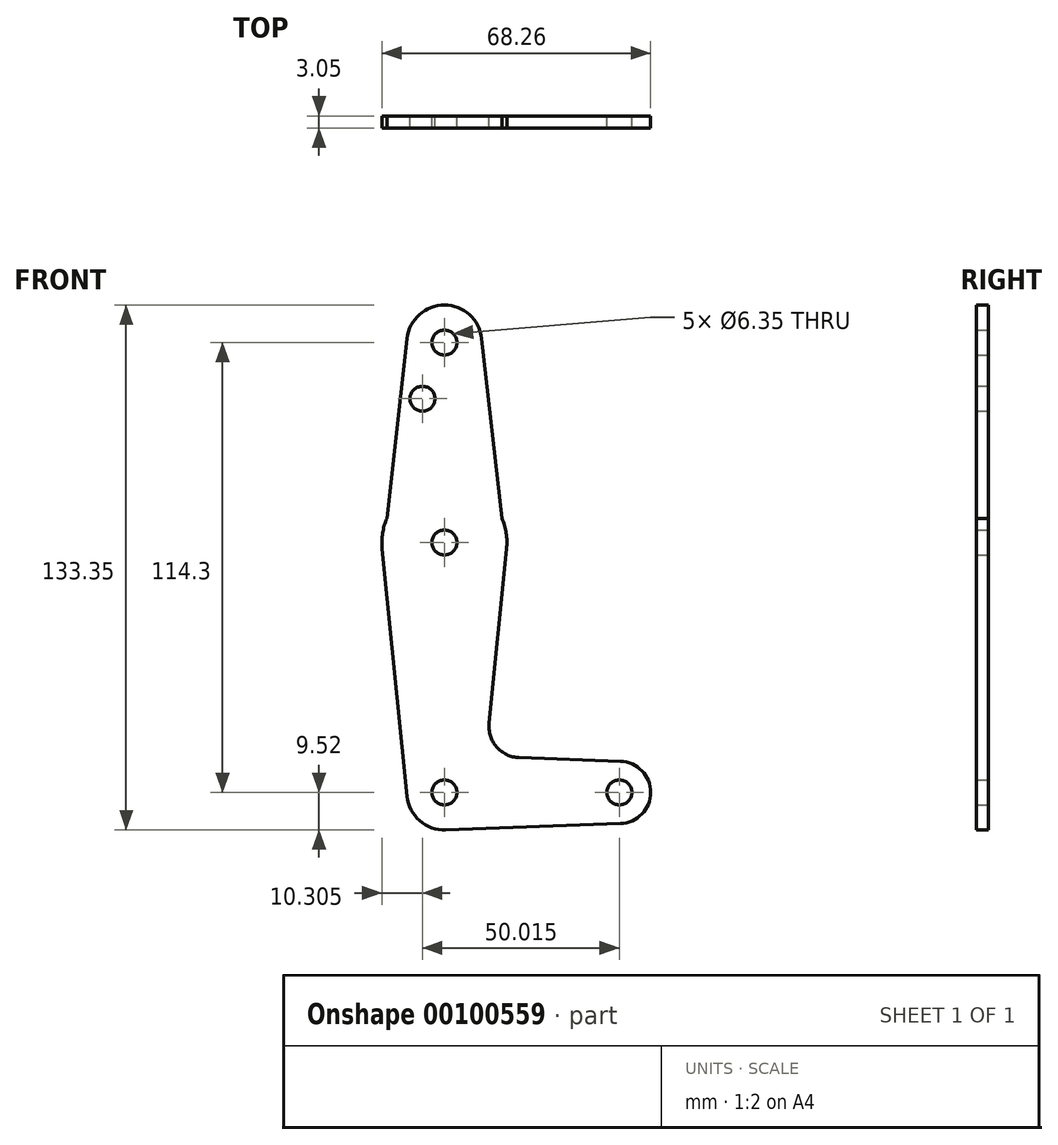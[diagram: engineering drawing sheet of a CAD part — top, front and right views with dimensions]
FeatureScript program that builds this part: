
annotation { "Feature Type Name" : "Feature", "Feature Type Description" : "" }
export const myFeature = defineFeature(function(context is Context, id is Id, definition is map)
    precondition{}
    {
        {
            var Q0;
            Q0=qCreatedBy(makeId("Front.planeOp"),FACE);
            var sketch = newSketch(context, id + "F0", { "sketchPlane" : qUnion([Q0])});
            skLineSegment(sketch, "E0", {"start": v(0, 0) * mm, "end": v(0, 114.3) * mm, "construction": true});
            skLineSegment(sketch, "E1", {"start": v(0, 0) * mm, "end": v(44.45, 0) * mm, "construction": true});
            skCircle(sketch, "E2", {"center": v(0, 114.3) * mm, "radius": 9.53 * mm});
            skCircle(sketch, "E3", {"center": v(0, 63.5) * mm, "radius": 15.88 * mm});
            skCircle(sketch, "E4", {"center": v(0, 0) * mm, "radius": 9.53 * mm});
            skCircle(sketch, "E5", {"center": v(44.45, 0) * mm, "radius": 7.94 * mm});
            skLineSegment(sketch, "E6", {"start": v(-9.46, 115.37) * mm, "end": v(-14.63, 69.66) * mm});
            skLineSegment(sketch, "E7", {"start": v(9.46, 115.37) * mm, "end": v(14.63, 69.66) * mm});
            skLineSegment(sketch, "E8", {"start": v(-9.48, -0.95) * mm, "end": v(-15.8, 61.91) * mm});
            skLineSegment(sketch, "E9", {"start": v(15.8, 61.91) * mm, "end": v(11.34, 17.6) * mm});
            skLineSegment(sketch, "E10", {"start": v(18.97, 8.85) * mm, "end": v(44.73, 7.93) * mm});
            skLineSegment(sketch, "E11", {"start": v(0.34, -9.52) * mm, "end": v(44.73, -7.93) * mm});
            skArc(sketch, "E12.filletArc", {"start": v(11.34, 17.6) * mm, "mid": v(13.26, 11.57) * mm, "end": v(18.97, 8.85) * mm});
            skCircle(sketch, "E13", {"center": v(0, 114.3) * mm, "radius": 3.18 * mm});
            skCircle(sketch, "E14", {"center": v(0, 63.5) * mm, "radius": 3.18 * mm});
            skCircle(sketch, "E15", {"center": v(0, 0) * mm, "radius": 3.18 * mm});
            skCircle(sketch, "E16", {"center": v(44.45, 0) * mm, "radius": 3.18 * mm});
            skCircle(sketch, "E17", {"center": v(-5.56, 100.03) * mm, "radius": 3.18 * mm});
            skSolve(sketch);
        }
        {
            var Q0;
            Q0 = qSketchRegion(id + "F0", true);
            extrude(context, id + "F1", {"entities" : qUnion([Q0]), "depth" : 3.05 * mm});
        }
    });
